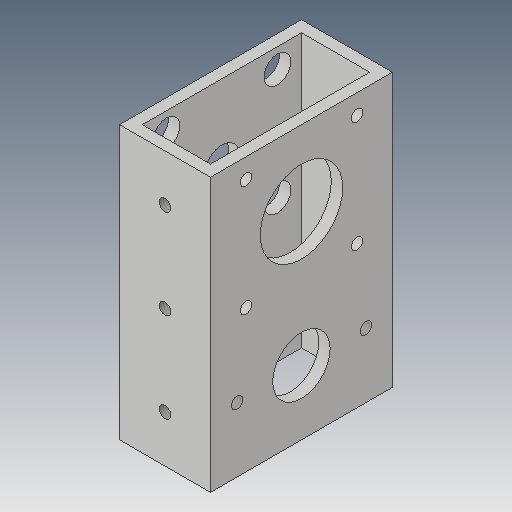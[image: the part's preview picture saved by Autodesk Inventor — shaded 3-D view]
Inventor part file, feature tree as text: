
AUTODESK INVENTOR PART (.ipt)
format: ipt  version: 2018 (Build 220112000, 112)  size: 179,712 bytes
history: native  units: mm
features: sketch x6, hole x4, extrude x3, other x3, shell x1, reference x1
ambient origin geometry x8: Origin, YZ Plane, XZ Plane, XY Plane, X Axis, Y Axis, Z Axis, Center Point
bodies: Solid1 (feature_tree)
feature tree (18):
  extrude  "Extrusion1"  Depth=25.4mm
  shell  "Shell1"  Thickness=76.2mm
  sketch  "Sketch2"  dims[d4=3.175mm d5=31.0mm]
  hole  "Hole1"  [1 undecoded]
  hole  "Hole2"  [1 undecoded]
  extrude  "Extrusion2"  Depth=8.0mm
  extrude  "Extrusion3"  Depth=50.8mm
  hole  "Hole4"  [1 undecoded]
  hole  "Hole5"  [1 undecoded]
  sketch  "Sketch1"  dims[d0=50.8mm d1=25.4mm d2=76.2mm d3=0.0mm]
  sketch  "Sketch3"  dims[d6=31.0mm d7=21.0mm]
  sketch  "Sketch4"  dims[d8=3.2mm d9=6.0mm d10=7.5mm d11=5.0mm d12=90.0deg d13=8.0mm d14=20.594885mm]
  sketch  "Sketch6"  dims[d15=10.0mm d16=6.0mm d17=6.5mm d18=3.0mm d19=90.0deg d20=8.0mm d21=20.594885mm d22=23.0mm]
  sketch  "Sketch7"  dims[d23=50.8mm d24=0.0mm d25=16.0mm d26=18.0mm d27=50.8mm d28=0.0mm d40=3.242mm d41=100.0mm d42=6.5mm d43=3.0mm d44=90.0deg d45=11.8mm d46=20.594885mm d47=36.0mm d48=3.242mm d49=100.0mm d50=6.5mm d51=3.0mm d52=90.0deg d53=11.8mm d54=20.594885mm d55=50.0mm]
  reference  "Reference1"
  parser-record x1  (decoder bookkeeping rows leaked as tree rows — omitted from the tree; the rows remain in map.json)
  other  "AMR_Transm2.iam"
  other  "7804K147_STAINLESS STEEL BALL BEARING:2"
note: 4 required parameter values undecoded (feature->parameter linkage not recoverable at this tier; creation-order binding heuristic only, values carry confidence <= 0.55)
note: 1 file-system path scrubbed to <path> (originals preserved in map.json)
